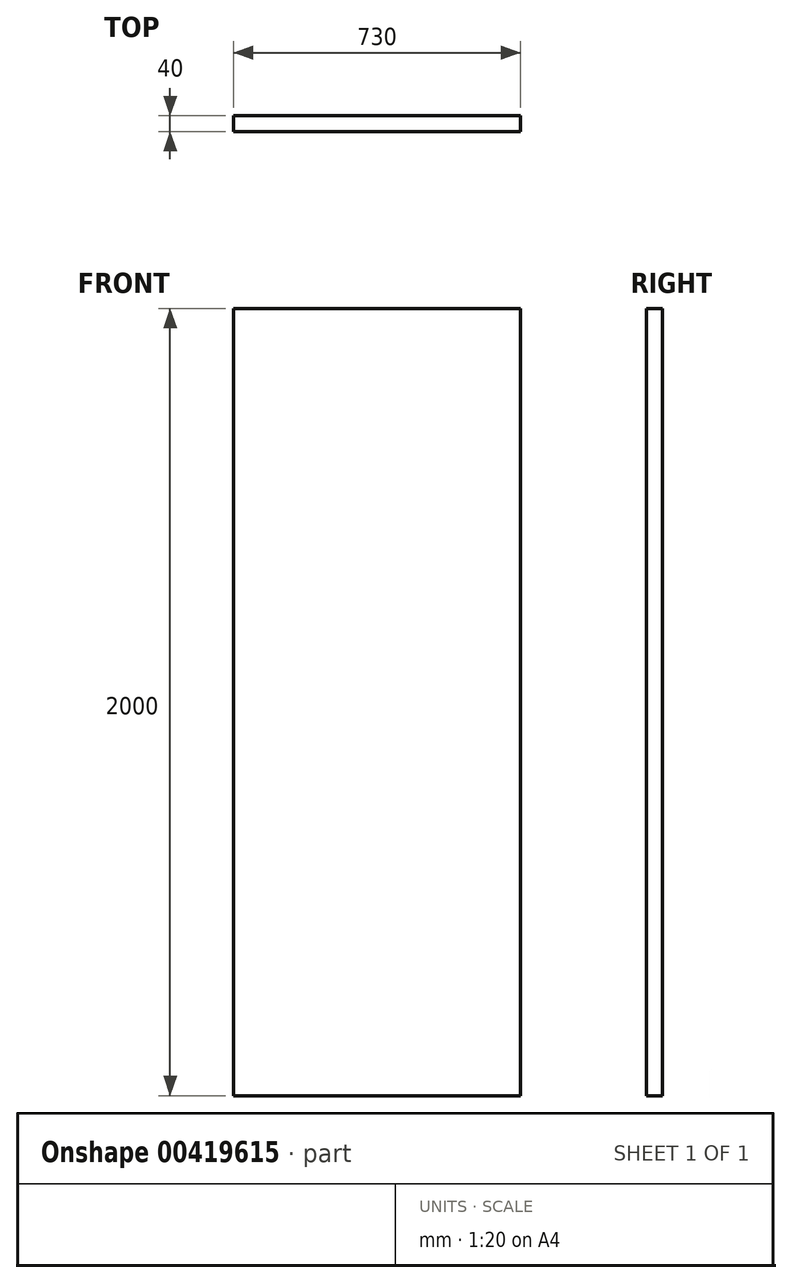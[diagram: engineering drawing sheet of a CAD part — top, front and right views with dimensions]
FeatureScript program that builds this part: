
annotation { "Feature Type Name" : "Feature", "Feature Type Description" : "" }
export const myFeature = defineFeature(function(context is Context, id is Id, definition is map)
    precondition{}
    {
        {
            var Q0;
            Q0=qCreatedBy(makeId("Top.planeOp"),FACE);
            var sketch = newSketch(context, id + "F0", { "sketchPlane" : qUnion([Q0])});
            skLineSegment(sketch, "E0.bottom", {"start": v(-58.14, -11.9) * mm, "end": v(671.86, -11.9) * mm});
            skLineSegment(sketch, "E0.top", {"start": v(-58.14, 28.1) * mm, "end": v(671.86, 28.1) * mm});
            skLineSegment(sketch, "E0.left", {"start": v(-58.14, -11.9) * mm, "end": v(-58.14, 28.1) * mm});
            skLineSegment(sketch, "E0.right", {"start": v(671.86, -11.9) * mm, "end": v(671.86, 28.1) * mm});
            skSolve(sketch);
        }
        {
            var Q0;
            Q0=makeQuery(id+"F0.imprint","IMPRINT",FACE,{"disambiguationData":[TD([[makeQuery(id+"F0.imprint","IMPRINT",EDGE,{"derivedFrom":sQuery(id+"F0.wireOp",EDGE,"E0.bottom")}),1.0]])]});
            extrude(context, id + "F1", {"entities" : qUnion([Q0]), "depth" : 2000 * mm});
        }
    });
